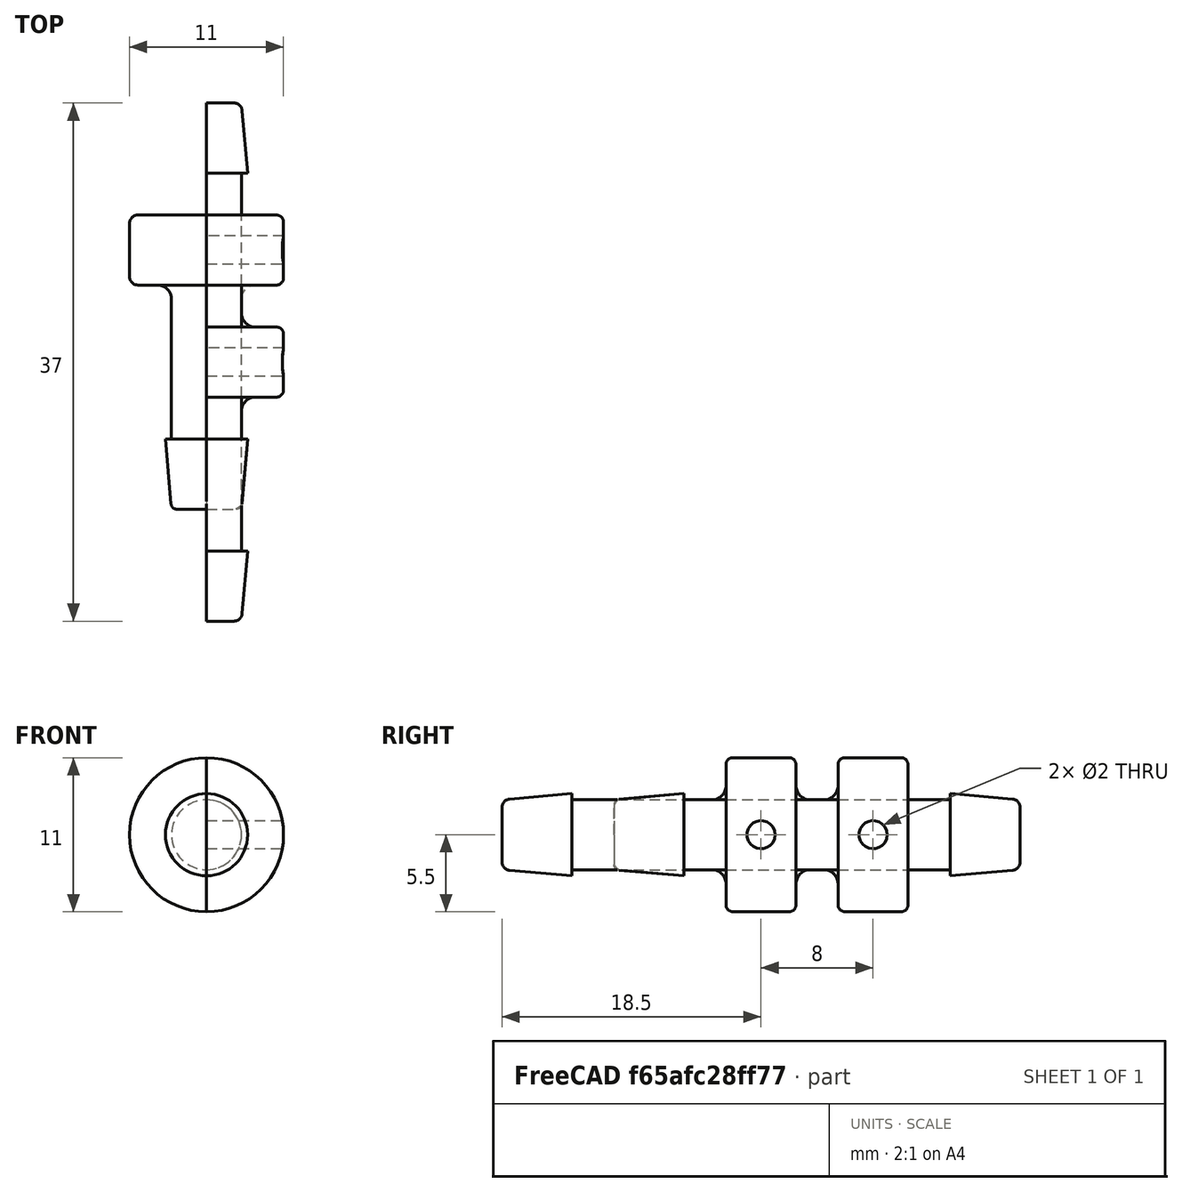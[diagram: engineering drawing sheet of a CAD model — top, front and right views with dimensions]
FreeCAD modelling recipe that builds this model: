
FCSTD DOCUMENT  (FreeCAD 0.19R24276 (Git))
Label: barb
License: All rights reserved
LicenseURL: http://en.wikipedia.org/wiki/All_rights_reserved
objects: PartDesign::Fillet×9, Sketcher::SketchObject×5, PartDesign::Revolution×3, PartDesign::Body×3, Mesh::Feature×3, PartDesign::Pocket×2, App::Part×1
note: 36 computed .brp shape members not serialized (recipe doc carries the construction recipe); baked Part::Feature solids carry a one-line shape summary decoded from their .brp

FEATURE [Sketcher::SketchObject] Sketch
  FullyConstrained = true
  MapMode = 5
  Placement = pos=(0,0,0) rot=(0.57735,0.57735,0.57735;2.0944rad)
  Support = -> [YZ_Plane001]
  sketch-geometry (8):
    g0: LineSegment StartX=-10.5 StartY=2.5 StartZ=0 EndX=-5.5 EndY=2.935 EndZ=0
    g1: LineSegment StartX=-5.5 StartY=2.935 StartZ=0 EndX=-5.5 EndY=2.5 EndZ=0
    g2: LineSegment StartX=-5.5 StartY=2.5 StartZ=0 EndX=5.5 EndY=2.5 EndZ=0
    g3: LineSegment StartX=10.5 StartY=0 StartZ=0 EndX=-10.5 EndY=-1.99758e-10 EndZ=0
    g4: LineSegment StartX=-10.5 StartY=-1.99758e-10 StartZ=0 EndX=-10.5 EndY=2.5 EndZ=0
    g5: LineSegment StartX=5.5 StartY=2.5 StartZ=0 EndX=5.5 EndY=5.5 EndZ=0
    g6: LineSegment StartX=5.5 StartY=5.5 StartZ=0 EndX=10.5 EndY=5.5 EndZ=0
    g7: LineSegment StartX=10.5 StartY=5.5 StartZ=0 EndX=10.5 EndY=0 EndZ=0
  constraints (23):
    c: Coincident(g0,g1)
    c: Vertical(g1)
    c: Coincident(g1,g2)
    c: Horizontal(g2)
    c: PointOnObject(g3,g-1)
    c: DistanceY(g-1,g0) = 2.935
    c: Coincident(g4,g3)
    c: Vertical(g4)
    c: DistanceY(g3,g4) = 2.5
    c: DistanceX(g0,g0) = 5
    c: DistanceY(g3,g2) = 2.5
    c: Coincident(g5,g2)
    c: Vertical(g5)
    c: Coincident(g5,g6)
    c: Horizontal(g6)
    c: Coincident(g6,g7)
    c: Coincident(g7,g3)
    c: Vertical(g7)
    c: DistanceX(g5,g6) = 5
    c: DistanceY(g3,g6) = 5.5
    c: Symmetric(g3,g3,g-1)
    c: Coincident(g4,g0)
    c: DistanceX(g3,g2) = 16
FEATURE [PartDesign::Revolution] Revolution
  Angle = 360
  Axis = (1e-16,1,-1e-16)
  Base = (0,0,0)
  Placement = pos=(0,0,0) rot=(0.57735,0.57735,0.57735;2.0944rad)
  Profile = -> Sketch
  ReferenceAxis = -> Y_Axis001
FEATURE [PartDesign::Fillet] Fillet
  Base = -> Revolution [Edge1]
  BaseFeature = -> Revolution
  Placement = pos=(0,0,0) rot=(0.57735,0.57735,0.57735;2.0944rad)
  Radius = 0.4
  SupportTransform = false
FEATURE [PartDesign::Fillet] Fillet001
  Base = -> Fillet [Edge7]
  BaseFeature = -> Fillet
  Placement = pos=(0,0,0) rot=(0.57735,0.57735,0.57735;2.0944rad)
  Radius = 1
  SupportTransform = false
FEATURE [PartDesign::Fillet] Fillet002
  Base = -> Fillet001 [Edge7,Edge10]
  BaseFeature = -> Fillet001
  Placement = pos=(0,0,0) rot=(0.57735,0.57735,0.57735;2.0944rad)
  Radius = 0.6
  SupportTransform = false
FEATURE [PartDesign::Body] Body  label="BodyFull"
  Group = -> [Sketch,Revolution,Fillet,Fillet001,Fillet002]
  Origin = -> Origin001
  Tip = -> Fillet002
FEATURE [Mesh::Feature] Mesh001  label="Fillet002 (Meshed)"
FEATURE [Sketcher::SketchObject] Sketch001
  FullyConstrained = true
  MapMode = 5
  Placement = pos=(0,0,0) rot=(0.57735,0.57735,0.57735;2.0944rad)
  Support = -> [YZ_Plane002]
  sketch-geometry (1):
    g0: Circle CenterX=8 CenterY=0 CenterZ=0 NormalX=0 NormalY=0 NormalZ=1 AngleXU=0 Radius=1
  constraints (3):
    c: Diameter(g0) = 2
    c: PointOnObject(g0,g-1)
    c: DistanceX(g-1,g0) = 8
FEATURE [Sketcher::SketchObject] Sketch002
  FullyConstrained = true
  MapMode = 5
  Placement = pos=(0,0,0) rot=(0.57735,0.57735,0.57735;2.0944rad)
  Support = -> [YZ_Plane002]
  sketch-geometry (8):
    g0: LineSegment StartX=-10.5 StartY=2.5 StartZ=0 EndX=-5.5 EndY=2.935 EndZ=0
    g1: LineSegment StartX=-5.5 StartY=2.935 StartZ=0 EndX=-5.5 EndY=2.5 EndZ=0
    g2: LineSegment StartX=-5.5 StartY=2.5 StartZ=0 EndX=5.5 EndY=2.5 EndZ=0
    g3: LineSegment StartX=10.5 StartY=0 StartZ=0 EndX=-10.5 EndY=-1.99758e-10 EndZ=0
    g4: LineSegment StartX=-10.5 StartY=-1.99758e-10 StartZ=0 EndX=-10.5 EndY=2.5 EndZ=0
    g5: LineSegment StartX=5.5 StartY=2.5 StartZ=0 EndX=5.5 EndY=5.5 EndZ=0
    g6: LineSegment StartX=5.5 StartY=5.5 StartZ=0 EndX=10.5 EndY=5.5 EndZ=0
    g7: LineSegment StartX=10.5 StartY=5.5 StartZ=0 EndX=10.5 EndY=0 EndZ=0
  constraints (23):
    c: Coincident(g0,g1)
    c: Vertical(g1)
    c: Coincident(g1,g2)
    c: Horizontal(g2)
    c: PointOnObject(g3,g-1)
    c: DistanceY(g-1,g0) = 2.935
    c: Coincident(g4,g3)
    c: Vertical(g4)
    c: DistanceY(g3,g4) = 2.5
    c: DistanceX(g0,g0) = 5
    c: DistanceY(g3,g2) = 2.5
    c: Coincident(g5,g2)
    c: Vertical(g5)
    c: Coincident(g5,g6)
    c: Horizontal(g6)
    c: Coincident(g6,g7)
    c: Coincident(g7,g3)
    c: Vertical(g7)
    c: DistanceX(g5,g6) = 5
    c: DistanceY(g3,g6) = 5.5
    c: Symmetric(g3,g3,g-1)
    c: Coincident(g4,g0)
    c: DistanceX(g3,g2) = 16
FEATURE [PartDesign::Revolution] Revolution001
  Angle = 180
  Axis = (1e-16,1,-1e-16)
  Base = (0,0,0)
  Placement = pos=(0,0,0) rot=(0.57735,0.57735,0.57735;2.0944rad)
  Profile = -> Sketch002
  ReferenceAxis = -> Y_Axis002
FEATURE [PartDesign::Fillet] Fillet003
  Base = -> Revolution001 [Edge1]
  BaseFeature = -> Revolution001
  Placement = pos=(0,0,0) rot=(0.57735,0.57735,0.57735;2.0944rad)
  Radius = 0.6
  SupportTransform = false
FEATURE [PartDesign::Fillet] Fillet004
  Base = -> Fillet003 [Edge22]
  BaseFeature = -> Fillet003
  Placement = pos=(0,0,0) rot=(0.57735,0.57735,0.57735;2.0944rad)
  Radius = 1
  SupportTransform = false
FEATURE [PartDesign::Fillet] Fillet005
  Base = -> Fillet004 [Edge18,Edge22]
  BaseFeature = -> Fillet004
  Placement = pos=(0,0,0) rot=(0.57735,0.57735,0.57735;2.0944rad)
  Radius = 0.5
  SupportTransform = false
FEATURE [PartDesign::Pocket] Pocket
  BaseFeature = -> Fillet005
  Length = 5
  Length2 = 100
  Midplane = true
  Placement = pos=(0,0,0) rot=(0.57735,0.57735,0.57735;2.0944rad)
  Profile = -> Sketch001
  Type = 1
FEATURE [PartDesign::Body] Body001  label="BodyHalf"
  Group = -> [Sketch002,Revolution001,Fillet003,Fillet004,Fillet005,Sketch001,Pocket]
  Origin = -> Origin002
  Tip = -> Pocket
FEATURE [Sketcher::SketchObject] Sketch003
  FullyConstrained = true
  MapMode = 5
  Placement = pos=(0,0,0) rot=(0.57735,0.57735,0.57735;2.0944rad)
  Support = -> [YZ_Plane003]
  sketch-geometry (1):
    g0: Circle CenterX=0 CenterY=0 CenterZ=0 NormalX=0 NormalY=0 NormalZ=1 AngleXU=0 Radius=1
  constraints (2):
    c: Diameter(g0) = 2
    c: Coincident(g0,g-1)
FEATURE [Sketcher::SketchObject] Sketch004
  FullyConstrained = true
  MapMode = 5
  Placement = pos=(0,0,0) rot=(0.57735,0.57735,0.57735;2.0944rad)
  Support = -> [YZ_Plane003]
  sketch-geometry (12):
    g0: LineSegment StartX=-18.5 StartY=2.5 StartZ=0 EndX=-13.5 EndY=2.935 EndZ=0
    g1: LineSegment StartX=-13.5 StartY=2.935 StartZ=0 EndX=-13.5 EndY=2.5 EndZ=0
    g2: LineSegment StartX=-13.5 StartY=2.5 StartZ=0 EndX=-2.5 EndY=2.5 EndZ=0
    g3: LineSegment StartX=18.5 StartY=0 StartZ=0 EndX=-18.5 EndY=0 EndZ=0
    g4: LineSegment StartX=-18.5 StartY=0 StartZ=0 EndX=-18.5 EndY=2.5 EndZ=0
    g5: LineSegment StartX=-2.5 StartY=2.5 StartZ=0 EndX=-2.5 EndY=5.5 EndZ=0
    g6: LineSegment StartX=-2.5 StartY=5.5 StartZ=0 EndX=2.5 EndY=5.5 EndZ=0
    g7: LineSegment StartX=2.5 StartY=5.5 StartZ=0 EndX=2.5 EndY=2.5 EndZ=0
    g8: LineSegment StartX=2.5 StartY=2.5 StartZ=0 EndX=13.5 EndY=2.5 EndZ=0
    g9: LineSegment StartX=13.5 StartY=2.5 StartZ=0 EndX=13.5 EndY=2.935 EndZ=0
    g10: LineSegment StartX=13.5 StartY=2.935 StartZ=0 EndX=18.5 EndY=2.5 EndZ=0
    g11: LineSegment StartX=18.5 StartY=2.5 StartZ=0 EndX=18.5 EndY=0 EndZ=0
  constraints (35):
    c: Coincident(g0,g1)
    c: Vertical(g1)
    c: Coincident(g1,g2)
    c: Horizontal(g2)
    c: PointOnObject(g3,g-1)
    c: DistanceY(g-1,g0) = 2.935
    c: Coincident(g4,g3)
    c: Vertical(g4)
    c: DistanceY(g3,g4) = 2.5
    c: DistanceX(g0,g0) = 5
    c: DistanceY(g3,g2) = 2.5
    c: Coincident(g5,g2)
    c: Vertical(g5)
    c: Coincident(g5,g6)
    c: Horizontal(g6)
    c: DistanceX(g5,g6) = 5
    c: DistanceY(g3,g6) = 5.5
    c: Symmetric(g3,g3,g-1)
    c: Coincident(g4,g0)
    c: DistanceX(g3,g2) = 16
    c: Coincident(g7,g6)
    c: Vertical(g7)
    c: Coincident(g8,g7)
    c: Horizontal(g8)
    c: Coincident(g9,g8)
    c: Coincident(g10,g9)
    c: Coincident(g11,g10)
    c: Vertical(g11)
    c: Coincident(g3,g11)
    c: Equal(g4,g11)
    c: Equal(g10,g0)
    c: Equal(g2,g8)
    c: Vertical(g9)
    c: Equal(g9,g1)
    c: Equal(g5,g7)
FEATURE [PartDesign::Revolution] Revolution002
  Angle = 180
  Axis = (1e-16,1,-1e-16)
  Base = (0,0,0)
  Placement = pos=(0,0,0) rot=(0.57735,0.57735,0.57735;2.0944rad)
  Profile = -> Sketch004
  ReferenceAxis = -> Y_Axis003
FEATURE [PartDesign::Fillet] Fillet006
  Base = -> Revolution002 [Edge1,Edge26]
  BaseFeature = -> Revolution002
  Placement = pos=(0,0,0) rot=(0.57735,0.57735,0.57735;2.0944rad)
  Radius = 0.6
  SupportTransform = false
FEATURE [PartDesign::Fillet] Fillet007
  Base = -> Fillet006 [Edge32,Edge37]
  BaseFeature = -> Fillet006
  Placement = pos=(0,0,0) rot=(0.57735,0.57735,0.57735;2.0944rad)
  Radius = 1
  SupportTransform = false
FEATURE [PartDesign::Fillet] Fillet008
  Base = -> Fillet007 [Edge24,Edge28]
  BaseFeature = -> Fillet007
  Placement = pos=(0,0,0) rot=(0.57735,0.57735,0.57735;2.0944rad)
  Radius = 0.5
  SupportTransform = false
FEATURE [PartDesign::Pocket] Pocket001
  BaseFeature = -> Fillet008
  Length = 5
  Length2 = 100
  Midplane = true
  Placement = pos=(0,0,0) rot=(0.57735,0.57735,0.57735;2.0944rad)
  Profile = -> Sketch003
  Type = 1
FEATURE [PartDesign::Body] Body002  label="BodyDouble"
  Group = -> [Sketch004,Revolution002,Sketch003,Fillet006,Fillet007,Fillet008,Pocket001]
  Origin = -> Origin003
  Tip = -> Pocket001
FEATURE [App::Part] Part
  Group = -> [Body,Body001,Body002]
  Origin = -> Origin
FEATURE [Mesh::Feature] Mesh002  label="Pocket001 (Meshed)"
FEATURE [Mesh::Feature] Mesh  label="Pocket (Meshed)"
